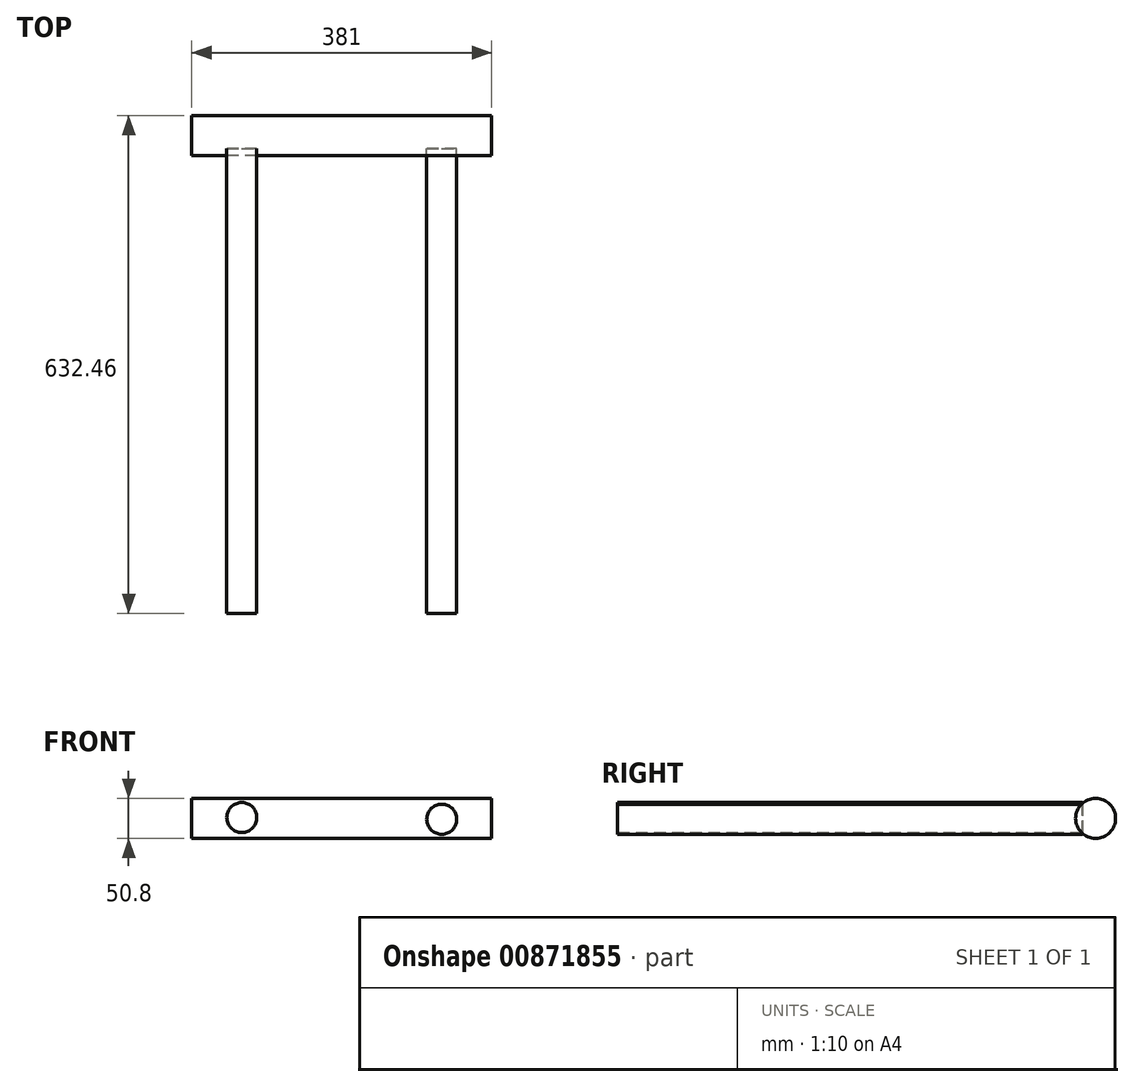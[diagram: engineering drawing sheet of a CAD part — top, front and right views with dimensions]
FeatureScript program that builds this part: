
annotation { "Feature Type Name" : "Feature", "Feature Type Description" : "" }
export const myFeature = defineFeature(function(context is Context, id is Id, definition is map)
    precondition{}
    {
        {
            var Q0;
            Q0=qCreatedBy(makeId("Front.planeOp"),FACE);
            var sketch = newSketch(context, id + "F0", { "sketchPlane" : qUnion([Q0])});
            skCircle(sketch, "E0", {"center": v(-127, 1.1) * mm, "radius": 19.05 * mm});
            skCircle(sketch, "E1", {"center": v(127, -1.1) * mm, "radius": 19.05 * mm});
            skLineSegment(sketch, "E2", {"start": v(-127, 1.1) * mm, "end": v(127, -1.1) * mm, "construction": true});
            skPoint(sketch, "E3", {"position": v(-107.95, 0.93) * mm});
            skPoint(sketch, "E4", {"position": v(107.95, -0.93) * mm});
            skSolve(sketch);
        }
        {
            var Q0;
            Q0=makeQuery(id+"F0.imprint","IMPRINT",FACE,{"disambiguationData":[TD([[makeQuery(id+"F0.imprint","IMPRINT",EDGE,{"derivedFrom":sQuery(id+"F0.wireOp",EDGE,"E0")}),1.0]])]});
            var Q1;
            Q1=makeQuery(id+"F0.imprint","IMPRINT",FACE,{"disambiguationData":[TD([[makeQuery(id+"F0.imprint","IMPRINT",EDGE,{"derivedFrom":sQuery(id+"F0.wireOp",EDGE,"E1")}),1.0]])]});
            extrude(context, id + "F1", {"entities" : qUnion([Q0, Q1]), "depth" : 590.55 * mm, "offsetDistance" : 25.4 * mm});
        }
        {
            var Q0;
            Q0=qCreatedBy(makeId("Right.planeOp"),FACE);
            var sketch = newSketch(context, id + "F2", { "sketchPlane" : qUnion([Q0])});
            skCircle(sketch, "E5", {"center": v(16.51, 0) * mm, "radius": 25.4 * mm});
            skSolve(sketch);
        }
        {
            var Q0;
            Q0=makeQuery(id+"F2.imprint","IMPRINT",FACE,{"disambiguationData":[TD([[makeQuery(id+"F2.imprint","IMPRINT",EDGE,{"derivedFrom":sQuery(id+"F2.wireOp",EDGE,"E5")}),1.0]])]});
            extrude(context, id + "F3", {"entities" : qUnion([Q0]), "endBound" : BoundingType.SYMMETRIC, "depth" : 381 * mm, "offsetDistance" : 25.4 * mm});
        }
    });
